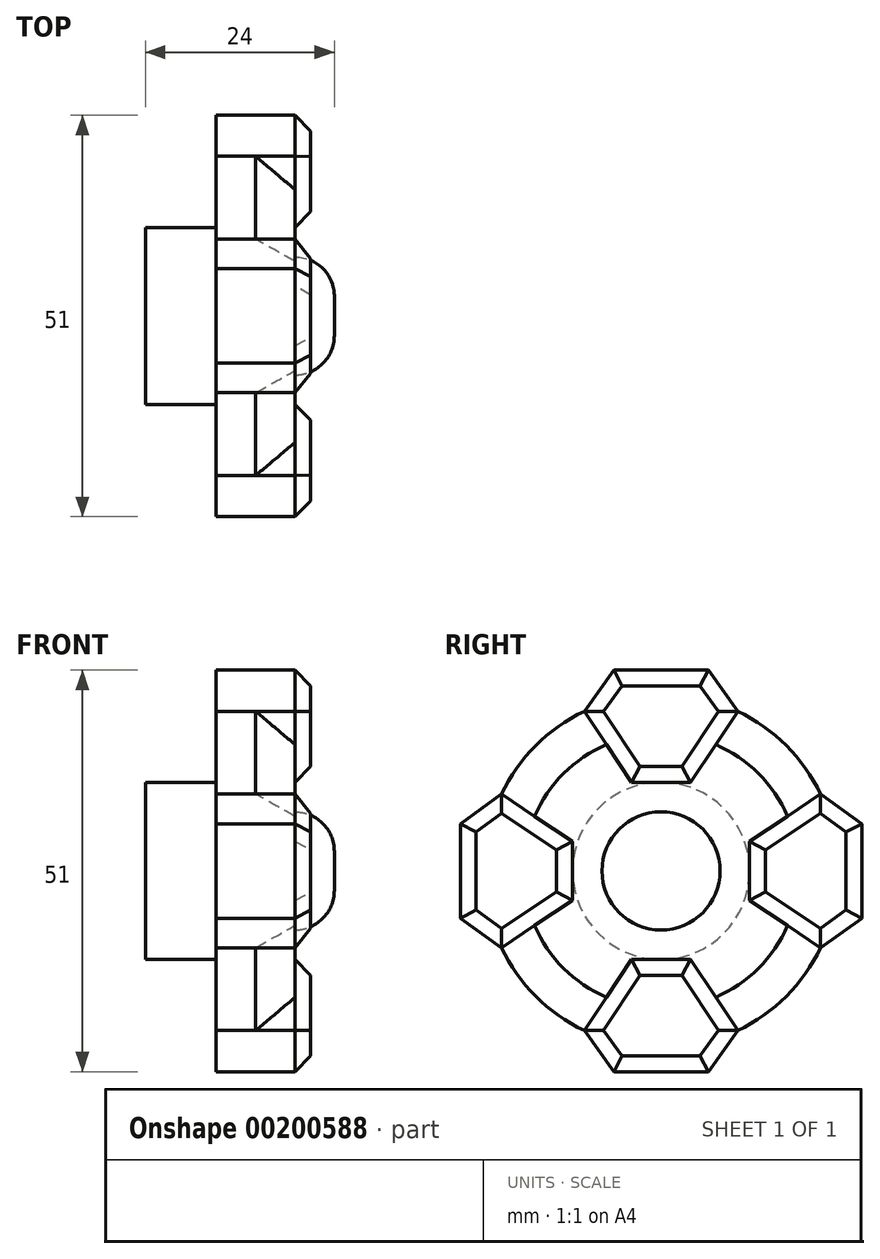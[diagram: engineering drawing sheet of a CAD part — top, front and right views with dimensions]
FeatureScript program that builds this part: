
annotation { "Feature Type Name" : "Feature", "Feature Type Description" : "" }
export const myFeature = defineFeature(function(context is Context, id is Id, definition is map)
    precondition{}
    {
        {
            var Q0;
            Q0=qCreatedBy(makeId("Right.planeOp"),FACE);
            var sketch = newSketch(context, id + "F0", { "sketchPlane" : qUnion([Q0])});
            skCircle(sketch, "E0", {"center": v(0, 0) * mm, "radius": 22.5 * mm});
            skLineSegment(sketch, "E1", {"start": v(0, 0) * mm, "end": v(0, 22.5) * mm, "construction": true});
            skLineSegment(sketch, "E2", {"start": v(0, 25.5) * mm, "end": v(-6, 25.5) * mm});
            skLineSegment(sketch, "E3", {"start": v(-6, 25.5) * mm, "end": v(-9.75, 20.28) * mm});
            skLineSegment(sketch, "E4", {"start": v(-9.75, 20.28) * mm, "end": v(-3.75, 11.25) * mm});
            skLineSegment(sketch, "E5", {"start": v(-3.75, 11.25) * mm, "end": v(0, 11.25) * mm});
            skLineSegment(sketch, "E6.MirrorCS", {"start": v(0, 25.5) * mm, "end": v(6, 25.5) * mm});
            skLineSegment(sketch, "E7.MirrorCS", {"start": v(6, 25.5) * mm, "end": v(9.75, 20.28) * mm});
            skLineSegment(sketch, "E8.MirrorCS", {"start": v(9.75, 20.28) * mm, "end": v(3.75, 11.25) * mm});
            skLineSegment(sketch, "E9.MirrorCS", {"start": v(3.75, 11.25) * mm, "end": v(0, 11.25) * mm});
            skPoint(sketch, "E10.center", {"position": v(-3.75, -3.75) * mm});
            skLineSegment(sketch, "E11.1.0", {"start": v(-25.5, 0) * mm, "end": v(-25.5, -6) * mm});
            skLineSegment(sketch, "E11.1.1", {"start": v(-25.5, 0) * mm, "end": v(-25.5, 6) * mm});
            skLineSegment(sketch, "E11.1.2", {"start": v(-25.5, 6) * mm, "end": v(-20.28, 9.75) * mm});
            skLineSegment(sketch, "E11.1.3", {"start": v(-25.5, -6) * mm, "end": v(-20.28, -9.75) * mm});
            skLineSegment(sketch, "E11.1.4", {"start": v(-20.28, -9.75) * mm, "end": v(-11.25, -3.75) * mm});
            skLineSegment(sketch, "E11.1.5", {"start": v(-11.25, -3.75) * mm, "end": v(-11.25, 0) * mm});
            skLineSegment(sketch, "E11.1.6", {"start": v(-11.25, 3.75) * mm, "end": v(-11.25, 0) * mm});
            skLineSegment(sketch, "E11.1.7", {"start": v(-20.28, 9.75) * mm, "end": v(-11.25, 3.75) * mm});
            skLineSegment(sketch, "E11.2.0", {"start": v(0, -25.5) * mm, "end": v(6, -25.5) * mm});
            skLineSegment(sketch, "E11.2.1", {"start": v(0, -25.5) * mm, "end": v(-6, -25.5) * mm});
            skLineSegment(sketch, "E11.2.2", {"start": v(-6, -25.5) * mm, "end": v(-9.75, -20.28) * mm});
            skLineSegment(sketch, "E11.2.3", {"start": v(6, -25.5) * mm, "end": v(9.75, -20.28) * mm});
            skLineSegment(sketch, "E11.2.4", {"start": v(9.75, -20.28) * mm, "end": v(3.75, -11.25) * mm});
            skLineSegment(sketch, "E11.2.5", {"start": v(3.75, -11.25) * mm, "end": v(0, -11.25) * mm});
            skLineSegment(sketch, "E11.2.6", {"start": v(-3.75, -11.25) * mm, "end": v(0, -11.25) * mm});
            skLineSegment(sketch, "E11.2.7", {"start": v(-9.75, -20.28) * mm, "end": v(-3.75, -11.25) * mm});
            skLineSegment(sketch, "E11.3.0", {"start": v(25.5, 0) * mm, "end": v(25.5, 6) * mm});
            skLineSegment(sketch, "E11.3.1", {"start": v(25.5, 0) * mm, "end": v(25.5, -6) * mm});
            skLineSegment(sketch, "E11.3.2", {"start": v(25.5, -6) * mm, "end": v(20.28, -9.75) * mm});
            skLineSegment(sketch, "E11.3.3", {"start": v(25.5, 6) * mm, "end": v(20.28, 9.75) * mm});
            skLineSegment(sketch, "E11.3.4", {"start": v(20.28, 9.75) * mm, "end": v(11.25, 3.75) * mm});
            skLineSegment(sketch, "E11.3.5", {"start": v(11.25, 3.75) * mm, "end": v(11.25, 0) * mm});
            skLineSegment(sketch, "E11.3.6", {"start": v(11.25, -3.75) * mm, "end": v(11.25, 0) * mm});
            skLineSegment(sketch, "E11.3.7", {"start": v(20.28, -9.75) * mm, "end": v(11.25, -3.75) * mm});
            skSolve(sketch);
        }
        {
            var Q0;
            {var subQ2=sQuery(id+"F0.wireOp",EDGE,"E4");Q0=makeQuery(id+"F0.imprint","IMPRINT",FACE,{"disambiguationData":[TD([[makeQuery(id+"F0.imprint","IMPRINT",EDGE,{"derivedFrom":subQ2}),-1.0]])]});}
            extrude(context, id + "F1", {"entities" : qUnion([Q0]), "depth" : 10 * mm});
        }
        {
            var Q0;
            {var subQ1=sQuery(id+"F0.wireOp",EDGE,"E4");Q0=makeQuery(id+"F0.imprint","IMPRINT",FACE,{"disambiguationData":[TD([[makeQuery(id+"F0.imprint","IMPRINT",EDGE,{"derivedFrom":subQ1}),1.0]])]});}
            var Q1;
            Q1=makeQuery(id+"F0.imprint","IMPRINT",FACE,{"disambiguationData":[TD([[makeQuery(id+"F0.imprint","IMPRINT",EDGE,{"derivedFrom":sQuery(id+"F0.wireOp",EDGE,"E2")}),1.0]])]});
            var Q2;
            {var subQ1=sQuery(id+"F0.wireOp",EDGE,"E11.1.4");Q2=makeQuery(id+"F0.imprint","IMPRINT",FACE,{"disambiguationData":[TD([[makeQuery(id+"F0.imprint","IMPRINT",EDGE,{"derivedFrom":subQ1}),1.0]])]});}
            var Q3;
            Q3=makeQuery(id+"F0.imprint","IMPRINT",FACE,{"disambiguationData":[TD([[makeQuery(id+"F0.imprint","IMPRINT",EDGE,{"derivedFrom":sQuery(id+"F0.wireOp",EDGE,"E11.1.0")}),1.0]])]});
            var Q4;
            {var subQ0=sQuery(id+"F0.wireOp",EDGE,"E11.2.4");Q4=makeQuery(id+"F0.imprint","IMPRINT",FACE,{"disambiguationData":[TD([[makeQuery(id+"F0.imprint","IMPRINT",EDGE,{"derivedFrom":subQ0}),1.0]])]});}
            var Q5;
            Q5=makeQuery(id+"F0.imprint","IMPRINT",FACE,{"disambiguationData":[TD([[makeQuery(id+"F0.imprint","IMPRINT",EDGE,{"derivedFrom":sQuery(id+"F0.wireOp",EDGE,"E11.2.0")}),1.0]])]});
            var Q6;
            {var subQ0=sQuery(id+"F0.wireOp",EDGE,"E11.3.4");Q6=makeQuery(id+"F0.imprint","IMPRINT",FACE,{"disambiguationData":[TD([[makeQuery(id+"F0.imprint","IMPRINT",EDGE,{"derivedFrom":subQ0}),1.0]])]});}
            var Q7;
            Q7=makeQuery(id+"F0.imprint","IMPRINT",FACE,{"disambiguationData":[TD([[makeQuery(id+"F0.imprint","IMPRINT",EDGE,{"derivedFrom":sQuery(id+"F0.wireOp",EDGE,"E11.3.0")}),1.0]])]});
            extrude(context, id + "F2", {"entities" : qUnion([Q0, Q1, Q2, Q3, Q4, Q5, Q6, Q7]), "operationType" : NewBodyOperationType.ADD, "depth" : 12 * mm});
        }
        {
            var Q0;
            {var subQ0=sQuery(id+"F0.wireOp",EDGE,"E0");Q0=makeQuery(id+"F1.opExtrude","CAP_EDGE",EDGE,{"disambiguationData":[OSD([subQ0]),TDD([makeQuery(id+"F0.imprint","IMPRINT",EDGE,{"disambiguationData":[TD([[makeQuery(id+"F0.imprint","INTERSECT",VERTEX,{"derivedFrom":[subQ0,sQuery(id+"F0.wireOp",EDGE,"E7.MirrorCS"),sQuery(id+"F0.wireOp",EDGE,"E8.MirrorCS")]}),1.0]])],"derivedFrom":subQ0})])],"isStart":false});}
            var Q1;
            {var subQ0=sQuery(id+"F0.wireOp",EDGE,"E0");Q1=makeQuery(id+"F1.opExtrude","CAP_EDGE",EDGE,{"disambiguationData":[OSD([subQ0]),TDD([makeQuery(id+"F0.imprint","IMPRINT",EDGE,{"disambiguationData":[TD([[makeQuery(id+"F0.imprint","INTERSECT",VERTEX,{"derivedFrom":[subQ0,sQuery(id+"F0.wireOp",EDGE,"E3"),sQuery(id+"F0.wireOp",EDGE,"E4")]}),-1.0]])],"derivedFrom":subQ0})])],"isStart":false});}
            var Q2;
            {var subQ0=sQuery(id+"F0.wireOp",EDGE,"E0");Q2=makeQuery(id+"F1.opExtrude","CAP_EDGE",EDGE,{"disambiguationData":[OSD([subQ0]),TDD([makeQuery(id+"F0.imprint","IMPRINT",EDGE,{"disambiguationData":[TD([[makeQuery(id+"F0.imprint","INTERSECT",VERTEX,{"derivedFrom":[subQ0,sQuery(id+"F0.wireOp",EDGE,"E10.1.3"),sQuery(id+"F0.wireOp",EDGE,"E10.1.4")]}),-1.0]])],"derivedFrom":subQ0})])],"isStart":false});}
            var Q3;
            {var subQ0=sQuery(id+"F0.wireOp",EDGE,"E0");Q3=makeQuery(id+"F1.opExtrude","CAP_EDGE",EDGE,{"disambiguationData":[OSD([subQ0]),TDD([makeQuery(id+"F0.imprint","IMPRINT",EDGE,{"disambiguationData":[TD([[makeQuery(id+"F0.imprint","INTERSECT",VERTEX,{"derivedFrom":[subQ0,sQuery(id+"F0.wireOp",EDGE,"E10.2.3"),sQuery(id+"F0.wireOp",EDGE,"E10.2.4")]}),-1.0]])],"derivedFrom":subQ0})])],"isStart":false});}
            chamfer(context, id + "F3", {"entities" : qUnion([Q0, Q1, Q2, Q3]), "width" : 5 * mm, "tangentPropagation" : true});
        }
        {
            var Q0;
            Q0=makeQuery(id+"F2.opExtrude","CAP_EDGE",EDGE,{"disambiguationData":[OSD([sQuery(id+"F0.wireOp",EDGE,"E2"),sQuery(id+"F0.wireOp",EDGE,"E6.MirrorCS")])],"isStart":false});
            var Q1;
            Q1=makeQuery(id+"F2.opExtrude","CAP_EDGE",EDGE,{"disambiguationData":[OSD([sQuery(id+"F0.wireOp",EDGE,"E3")])],"isStart":false});
            var Q2;
            Q2=makeQuery(id+"F2.opExtrude","CAP_EDGE",EDGE,{"disambiguationData":[OSD([sQuery(id+"F0.wireOp",EDGE,"E7.MirrorCS")])],"isStart":false});
            var Q3;
            Q3=makeQuery(id+"F2.opExtrude","CAP_EDGE",EDGE,{"disambiguationData":[OSD([sQuery(id+"F0.wireOp",EDGE,"E4")])],"isStart":false});
            var Q4;
            Q4=makeQuery(id+"F2.opExtrude","CAP_EDGE",EDGE,{"disambiguationData":[OSD([sQuery(id+"F0.wireOp",EDGE,"E8.MirrorCS")])],"isStart":false});
            var Q5;
            Q5=makeQuery(id+"F2.opExtrude","CAP_EDGE",EDGE,{"disambiguationData":[OSD([sQuery(id+"F0.wireOp",EDGE,"E5"),sQuery(id+"F0.wireOp",EDGE,"E9.MirrorCS")])],"isStart":false});
            var Q6;
            Q6=makeQuery(id+"F2.opExtrude","CAP_EDGE",EDGE,{"disambiguationData":[OSD([sQuery(id+"F0.wireOp",EDGE,"E11.1.7")])],"isStart":false});
            var Q7;
            Q7=makeQuery(id+"F2.opExtrude","CAP_EDGE",EDGE,{"disambiguationData":[OSD([sQuery(id+"F0.wireOp",EDGE,"E11.1.2")])],"isStart":false});
            var Q8;
            Q8=makeQuery(id+"F2.opExtrude","CAP_EDGE",EDGE,{"disambiguationData":[OSD([sQuery(id+"F0.wireOp",EDGE,"E11.1.0"),sQuery(id+"F0.wireOp",EDGE,"E11.1.1")])],"isStart":false});
            var Q9;
            Q9=makeQuery(id+"F2.opExtrude","CAP_EDGE",EDGE,{"disambiguationData":[OSD([sQuery(id+"F0.wireOp",EDGE,"E11.1.3")])],"isStart":false});
            var Q10;
            Q10=makeQuery(id+"F2.opExtrude","CAP_EDGE",EDGE,{"disambiguationData":[OSD([sQuery(id+"F0.wireOp",EDGE,"E11.1.4")])],"isStart":false});
            var Q11;
            Q11=makeQuery(id+"F2.opExtrude","CAP_EDGE",EDGE,{"disambiguationData":[OSD([sQuery(id+"F0.wireOp",EDGE,"E11.1.5"),sQuery(id+"F0.wireOp",EDGE,"E11.1.6")])],"isStart":false});
            var Q12;
            Q12=makeQuery(id+"F2.opExtrude","CAP_EDGE",EDGE,{"disambiguationData":[OSD([sQuery(id+"F0.wireOp",EDGE,"E11.2.5"),sQuery(id+"F0.wireOp",EDGE,"E11.2.6")])],"isStart":false});
            var Q13;
            Q13=makeQuery(id+"F2.opExtrude","CAP_EDGE",EDGE,{"disambiguationData":[OSD([sQuery(id+"F0.wireOp",EDGE,"E11.2.7")])],"isStart":false});
            var Q14;
            Q14=makeQuery(id+"F2.opExtrude","CAP_EDGE",EDGE,{"disambiguationData":[OSD([sQuery(id+"F0.wireOp",EDGE,"E11.2.2")])],"isStart":false});
            var Q15;
            Q15=makeQuery(id+"F2.opExtrude","CAP_FACE",FACE,{"disambiguationData":[OSD([sQuery(id+"F0.wireOp",EDGE,"E11.2.0"),sQuery(id+"F0.wireOp",EDGE,"E11.2.1"),sQuery(id+"F0.wireOp",EDGE,"E11.2.2"),sQuery(id+"F0.wireOp",EDGE,"E11.2.3"),sQuery(id+"F0.wireOp",EDGE,"E11.2.4"),sQuery(id+"F0.wireOp",EDGE,"E11.2.5"),sQuery(id+"F0.wireOp",EDGE,"E11.2.6"),sQuery(id+"F0.wireOp",EDGE,"E11.2.7")])],"isStart":false});
            var Q16;
            Q16=makeQuery(id+"F2.opExtrude","CAP_EDGE",EDGE,{"disambiguationData":[OSD([sQuery(id+"F0.wireOp",EDGE,"E11.3.7")])],"isStart":false});
            var Q17;
            Q17=makeQuery(id+"F2.opExtrude","CAP_EDGE",EDGE,{"disambiguationData":[OSD([sQuery(id+"F0.wireOp",EDGE,"E11.3.5"),sQuery(id+"F0.wireOp",EDGE,"E11.3.6")])],"isStart":false});
            var Q18;
            Q18=makeQuery(id+"F2.opExtrude","CAP_EDGE",EDGE,{"disambiguationData":[OSD([sQuery(id+"F0.wireOp",EDGE,"E11.3.4")])],"isStart":false});
            var Q19;
            Q19=makeQuery(id+"F2.opExtrude","CAP_EDGE",EDGE,{"disambiguationData":[OSD([sQuery(id+"F0.wireOp",EDGE,"E11.3.3")])],"isStart":false});
            var Q20;
            Q20=makeQuery(id+"F2.opExtrude","CAP_EDGE",EDGE,{"disambiguationData":[OSD([sQuery(id+"F0.wireOp",EDGE,"E11.3.0"),sQuery(id+"F0.wireOp",EDGE,"E11.3.1")])],"isStart":false});
            var Q21;
            Q21=makeQuery(id+"F2.opExtrude","CAP_EDGE",EDGE,{"disambiguationData":[OSD([sQuery(id+"F0.wireOp",EDGE,"E11.3.2")])],"isStart":false});
            chamfer(context, id + "F4", {"entities" : qUnion([Q0, Q1, Q2, Q3, Q4, Q5, Q6, Q7, Q8, Q9, Q10, Q11, Q12, Q13, Q14, Q15, Q16, Q17, Q18, Q19, Q20, Q21]), "width" : 2 * mm, "tangentPropagation" : true});
        }
        {
            var Q0;
            Q0=makeQuery(id+"F1.opExtrude","CAP_FACE",FACE,{"disambiguationData":[OSD([sQuery(id+"F0.wireOp",EDGE,"E0"),sQuery(id+"F0.wireOp",EDGE,"E4"),sQuery(id+"F0.wireOp",EDGE,"E5"),sQuery(id+"F0.wireOp",EDGE,"E8.MirrorCS"),sQuery(id+"F0.wireOp",EDGE,"E9.MirrorCS"),sQuery(id+"F0.wireOp",EDGE,"E10.1.4"),sQuery(id+"F0.wireOp",EDGE,"E10.1.5"),sQuery(id+"F0.wireOp",EDGE,"E10.1.6"),sQuery(id+"F0.wireOp",EDGE,"E10.1.7"),sQuery(id+"F0.wireOp",EDGE,"E10.2.4"),sQuery(id+"F0.wireOp",EDGE,"E10.2.5"),sQuery(id+"F0.wireOp",EDGE,"E10.2.6"),sQuery(id+"F0.wireOp",EDGE,"E10.2.7"),sQuery(id+"F0.wireOp",EDGE,"E10.3.4"),sQuery(id+"F0.wireOp",EDGE,"E10.3.5"),sQuery(id+"F0.wireOp",EDGE,"E10.3.6"),sQuery(id+"F0.wireOp",EDGE,"E10.3.7")])],"isStart":false});
            var sketch = newSketch(context, id + "F5", { "sketchPlane" : qUnion([Q0])});
            skCircle(sketch, "E12", {"center": v(0, 0) * mm, "radius": 7.5 * mm});
            skSolve(sketch);
        }
        {
            var Q0;
            Q0=makeQuery(id+"F5.imprint","IMPRINT",FACE,{"disambiguationData":[TD([[makeQuery(id+"F5.imprint","IMPRINT",EDGE,{"derivedFrom":sQuery(id+"F5.wireOp",EDGE,"E12")}),1.0]])]});
            extrude(context, id + "F6", {"entities" : qUnion([Q0]), "depth" : 5 * mm});
        }
        {
            var Q0;
            Q0=makeQuery(id+"F6.opExtrude","CAP_EDGE",EDGE,{"disambiguationData":[OSD([sQuery(id+"F5.wireOp",EDGE,"E12")])],"isStart":false});
            fillet(context, id + "F7", {"entities" : qUnion([Q0]), "radius" : 5 * mm, "tangentPropagation" : true, "allowEdgeOverflow" : false});
        }
        {
            var Q0;
            {var subQ2=sQuery(id+"F0.wireOp",EDGE,"E4");Q0=makeQuery(id+"F0.imprint","IMPRINT",FACE,{"disambiguationData":[TD([[makeQuery(id+"F0.imprint","IMPRINT",EDGE,{"derivedFrom":subQ2}),-1.0]])]});}
            var sketch = newSketch(context, id + "F8", { "sketchPlane" : qUnion([Q0])});
            skCircle(sketch, "E13", {"center": v(0, 0) * mm, "radius": 11.25 * mm});
            skSolve(sketch);
        }
        {
            var Q0;
            {var subQ0=sQuery(id+"F8.wireOp",EDGE,"E13");var subQ1=makeQuery(id+"F8.imprint","INTERSECT",VERTEX,{"derivedFrom":[makeQuery(id+"F0.imprint","IMPRINT",EDGE,{"derivedFrom":sQuery(id+"F0.wireOp",EDGE,"E5")}),makeQuery(id+"F0.imprint","IMPRINT",EDGE,{"derivedFrom":sQuery(id+"F0.wireOp",EDGE,"E9.MirrorCS")}),subQ0]});Q0=makeQuery(id+"F8.imprint","IMPRINT",FACE,{"disambiguationData":[TD([[makeQuery(id+"F8.imprint","IMPRINT",EDGE,{"disambiguationData":[TD([[subQ1,1.0]])],"derivedFrom":subQ0}),1.0]])]});}
            extrude(context, id + "F9", {"entities" : qUnion([Q0]), "operationType" : NewBodyOperationType.ADD, "oppositeDirection" : true, "depth" : 9 * mm});
        }
    });
